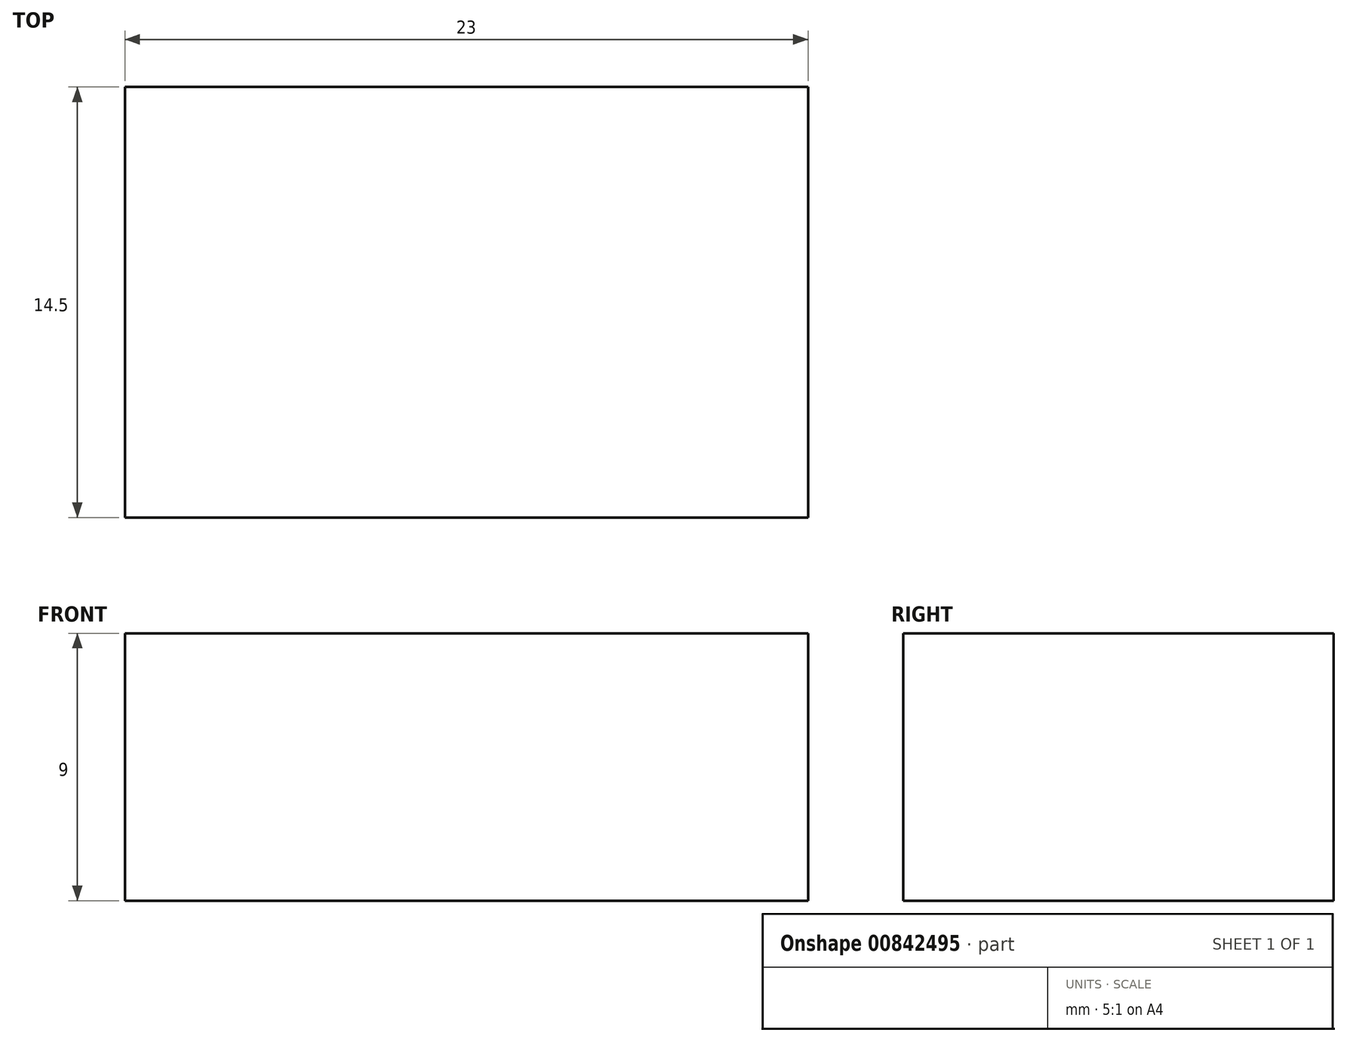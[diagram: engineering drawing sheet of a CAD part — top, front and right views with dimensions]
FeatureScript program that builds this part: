
annotation { "Feature Type Name" : "Feature", "Feature Type Description" : "" }
export const myFeature = defineFeature(function(context is Context, id is Id, definition is map)
    precondition{}
    {
        {
            var Q0;
            Q0=qCreatedBy(makeId("Top.planeOp"),FACE);
            var sketch = newSketch(context, id + "F0", { "sketchPlane" : qUnion([Q0])});
            skLineSegment(sketch, "E0.bottom", {"start": v(-23, 0) * mm, "end": v(0, 0) * mm});
            skLineSegment(sketch, "E0.top", {"start": v(-23, 14.5) * mm, "end": v(0, 14.5) * mm});
            skLineSegment(sketch, "E0.left", {"start": v(-23, 0) * mm, "end": v(-23, 14.5) * mm});
            skLineSegment(sketch, "E0.right", {"start": v(0, 0) * mm, "end": v(0, 14.5) * mm});
            skSolve(sketch);
        }
        {
            var Q0;
            Q0=qSketchRegion(id+"F0",true);
            extrude(context, id + "F1", {"entities" : qUnion([Q0]), "depth" : 9 * mm, "offsetDistance" : 25 * mm});
        }
    });
